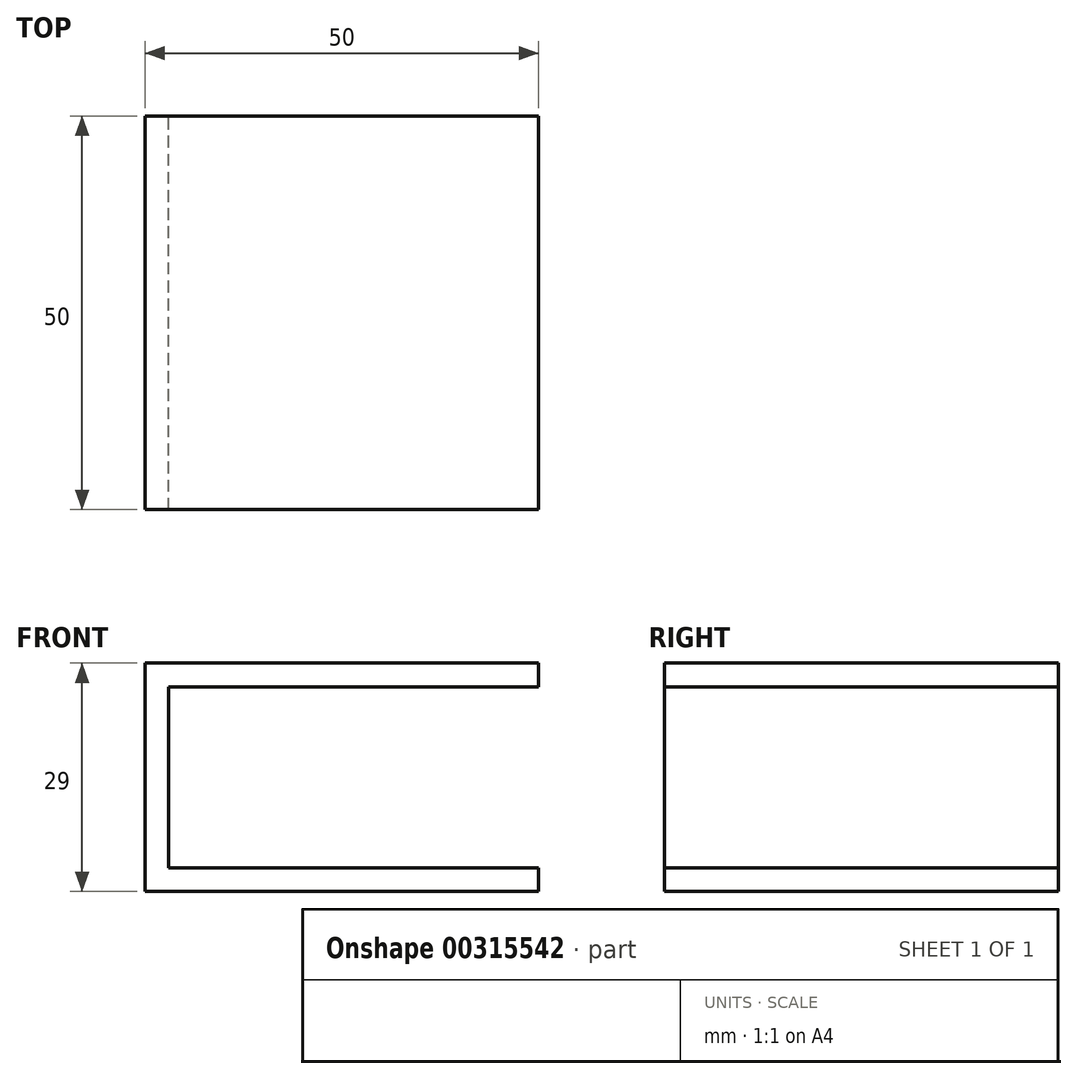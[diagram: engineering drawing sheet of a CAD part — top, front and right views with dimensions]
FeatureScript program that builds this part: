
annotation { "Feature Type Name" : "Feature", "Feature Type Description" : "" }
export const myFeature = defineFeature(function(context is Context, id is Id, definition is map)
    precondition{}
    {
        {
            var Q0;
            Q0=qCreatedBy(makeId("Front.planeOp"),FACE);
            var sketch = newSketch(context, id + "F0", { "sketchPlane" : qUnion([Q0])});
            skPoint(sketch, "E0.middle", {"position": v(0, 0) * mm});
            skLineSegment(sketch, "E1.bottom", {"start": v(-25, -14.5) * mm, "end": v(25, -14.5) * mm});
            skLineSegment(sketch, "E1.top", {"start": v(-25, 14.5) * mm, "end": v(25, 14.5) * mm});
            skLineSegment(sketch, "E1.left", {"start": v(-25, -14.5) * mm, "end": v(-25, 14.5) * mm});
            skLineSegment(sketch, "E2.bottom", {"start": v(25, -11.5) * mm, "end": v(-22, -11.5) * mm});
            skLineSegment(sketch, "E2.top", {"start": v(25, 11.5) * mm, "end": v(-22, 11.5) * mm});
            skLineSegment(sketch, "E2.right", {"start": v(-22, -11.5) * mm, "end": v(-22, 11.5) * mm});
            skPoint(sketch, "E2.middle", {"position": v(1.5, 0) * mm});
            skLineSegment(sketch, "E3", {"start": v(25, 11.5) * mm, "end": v(25, 14.5) * mm});
            skLineSegment(sketch, "E4", {"start": v(25, -14.5) * mm, "end": v(25, -11.5) * mm});
            skSolve(sketch);
        }
        {
            var Q0;
            Q0=makeQuery(id+"F0.imprint","IMPRINT",FACE,{"disambiguationData":[TD([[makeQuery(id+"F0.imprint","IMPRINT",EDGE,{"derivedFrom":sQuery(id+"F0.wireOp",EDGE,"E1.bottom")}),1.0]])]});
            extrude(context, id + "F1", {"entities" : qUnion([Q0]), "endBound" : BoundingType.SYMMETRIC, "depth" : 50 * mm});
        }
    });
